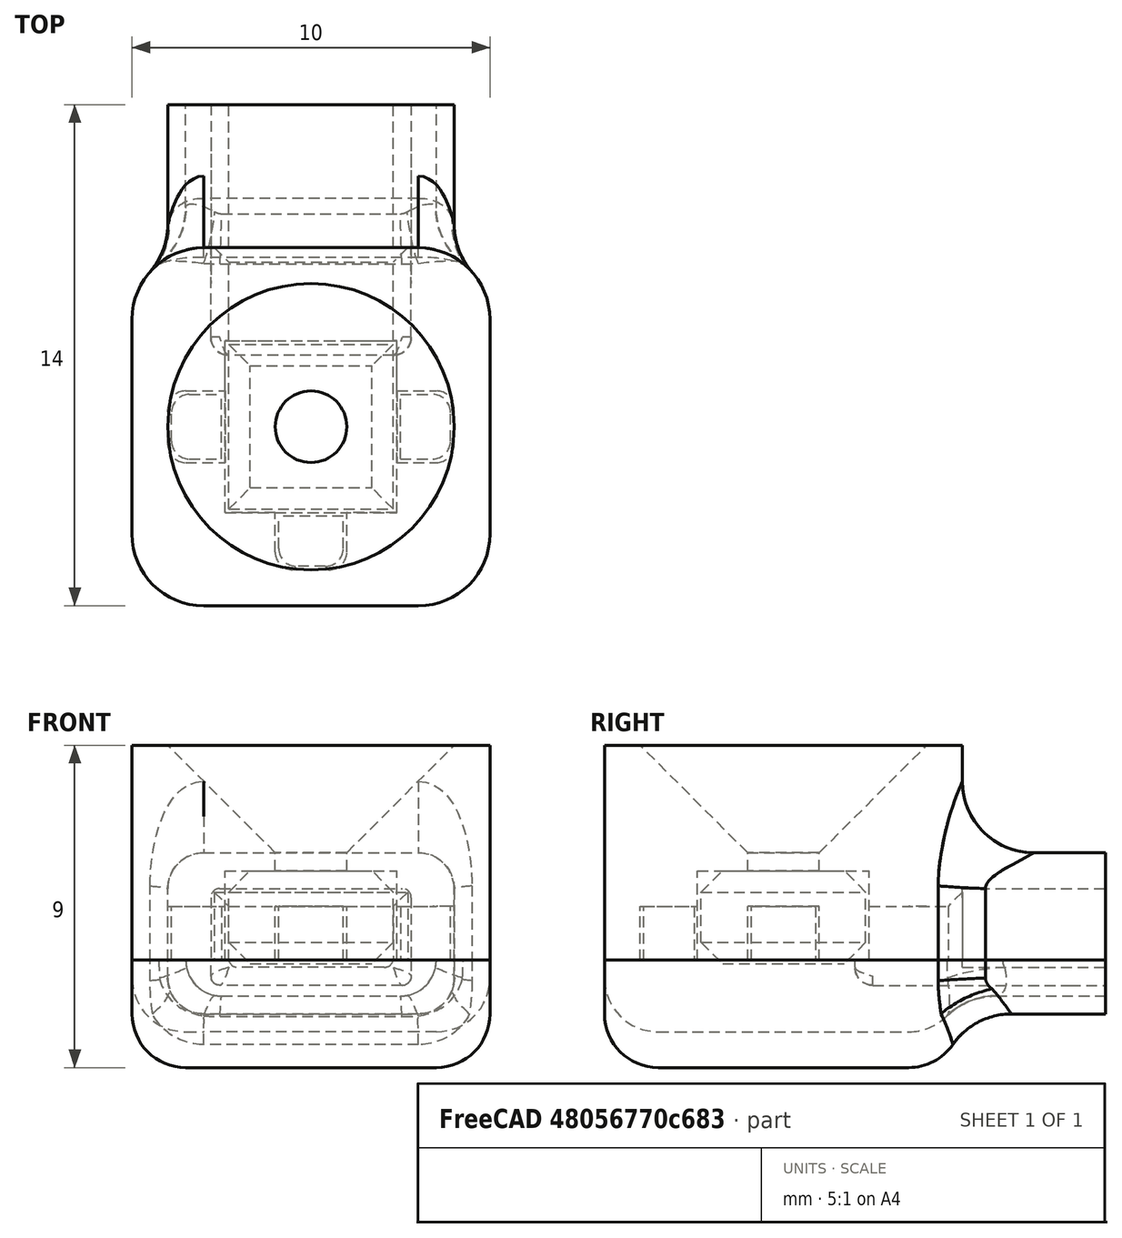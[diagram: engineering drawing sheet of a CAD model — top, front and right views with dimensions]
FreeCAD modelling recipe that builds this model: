
FCSTD DOCUMENT  (FreeCAD 0.18R16110 (Git))
Label: PhotodidoeHolder_APM_v4
License: All rights reserved
LicenseURL: http://en.wikipedia.org/wiki/All_rights_reserved
objects: Part::Box×24, Part::Fillet×22, Part::Cut×14, Part::MultiFuse×8, Part::Chamfer×2, Part::Cone×1, Part::Cylinder×1
note: 72 computed .brp shape members not serialized (recipe doc carries the construction recipe); baked Part::Feature solids carry a one-line shape summary decoded from their .brp

FEATURE [Part::Cone] Cone
  Angle = 360
  AttacherType = Attacher::AttachEngine3D
  Height = 3
  Radius1 = 1
  Radius2 = 4
FEATURE [Part::Box] Box  label="Cube"
  AttacherType = Attacher::AttachEngine3D
  Height = 3.5
  Length = 4.8
  Placement = pos=(-2.4,-2.4,-4) rot=(0,0,1;0rad)
  Width = 4.8
FEATURE [Part::Box] Box001  label="Cube001"
  AttacherType = Attacher::AttachEngine3D
  Height = 6
  Length = 10
  Placement = pos=(-5,-5,-3) rot=(0,0,1;0rad)
  Width = 10
FEATURE [Part::MultiFuse] Fusion
  Shapes = -> [Box,Cone]
FEATURE [Part::Cut] Cut
  Base = -> Box001
  Tool = -> Fusion
FEATURE [Part::Box] Box002  label="Cube002"
  AttacherType = Attacher::AttachEngine3D
  Height = 2
  Length = 4.6
  Placement = pos=(-2.3,2.4,-3.5) rot=(0,0,1;0rad)
  Width = 5
FEATURE [Part::Cut] Cut001
  Base = -> Cut
  Tool = -> Box002
FEATURE [Part::Fillet] Fillet
  Base = -> Cut001
  Edges = 4 edges r=2: [Edge1,Edge3,Edge6,Edge16]
FEATURE [Part::Cylinder] Cylinder
  Angle = 360
  AttacherType = Attacher::AttachEngine3D
  Height = 10
  Placement = pos=(0,0,-3) rot=(0,0,1;0rad)
  Radius = 1
FEATURE [Part::Cut] Cut002
  Base = -> Fillet
  Tool = -> Cylinder
FEATURE [Part::Box] Box003  label="Cube003"
  AttacherType = Attacher::AttachEngine3D
  Height = 3
  Length = 10
  Placement = pos=(-5,-5,-6) rot=(0,0,1;0rad)
  Width = 10
FEATURE [Part::Fillet] Fillet001
  Base = -> Box003
  Edges = 4 edges r=2: [Edge1,Edge3,Edge5,Edge7]
FEATURE [Part::Box] Box005  label="Diode"
  AttacherType = Attacher::AttachEngine3D
  Height = 2.6
  Length = 4.6
  Placement = pos=(-2.3,-2.3,-3) rot=(0,0,1;0rad)
  Width = 4.6
FEATURE [Part::Chamfer] Chamfer  label="Photodiode"
  Base = -> Box005
  Edges = 8 edges r=0.6: [Edge2,Edge4,Edge6,Edge8,Edge9,Edge10,Edge11,Edge12]
  Placement = pos=(0,0,-0.1) rot=(0,0,1;0rad)
FEATURE [Part::Fillet] Fillet003
  Base = -> Fillet001
  Edges = 8 edges r=1.5: [Edge4,Edge12,Edge14,Edge16,Edge17,Edge18,Edge19,Edge20]
FEATURE [Part::Box] Box007  label="Cube006"
  AttacherType = Attacher::AttachEngine3D
  Height = 1.5
  Length = 8
  Placement = pos=(-4,-1,-3) rot=(0,0,1;0rad)
  Width = 2
FEATURE [Part::Fillet] Fillet004
  Base = -> Box007
  Edges = 4 edges r=0.5: [Edge1,Edge3,Edge5,Edge7]
FEATURE [Part::Cut] Cut004
  Base = -> Cut002
  Tool = -> Fillet004
FEATURE [Part::Box] Box008  label="Cube007"
  AttacherType = Attacher::AttachEngine3D
  Height = 1.5
  Length = 7.8
  Placement = pos=(-3.9,-0.9,-3) rot=(0,0,1;0rad)
  Width = 1.8
FEATURE [Part::Fillet] Fillet005
  Base = -> Box008
  Edges = 4 edges r=0.5: [Edge1,Edge3,Edge5,Edge7]
FEATURE [Part::Box] Box009  label="Cube008"
  AttacherType = Attacher::AttachEngine3D
  Height = 1.5
  Length = 7.8
  Placement = pos=(-3.9,-0.9,-3) rot=(0,0,1;0rad)
  Width = 1.8
FEATURE [Part::Fillet] Fillet006
  Base = -> Box009
  Edges = 4 edges r=0.5: [Edge1,Edge3,Edge5,Edge7]
  Placement = pos=(0,0,0) rot=(0,0,1;1.5708rad)
FEATURE [Part::MultiFuse] Fusion001
  Shapes = -> [Fillet006,Fillet005]
FEATURE [Part::Box] Box010  label="Cube009"
  AttacherType = Attacher::AttachEngine3D
  Height = 5
  Length = 5
  Placement = pos=(-2.5,-2.5,-4) rot=(0,0,1;0rad)
  Width = 7
FEATURE [Part::Cut] Cut005
  Base = -> Fusion001
  Tool = -> Box010
FEATURE [Part::MultiFuse] Fusion002  label="Back"
  Shapes = -> [Fillet003,Cut005]
FEATURE [Part::Box] Box011  label="Cube010"
  AttacherType = Attacher::AttachEngine3D
  Height = 1.5
  Length = 8
  Placement = pos=(-4,-1,-3) rot=(0,0,1;0rad)
  Width = 2
FEATURE [Part::Fillet] Fillet007
  Base = -> Box011
  Edges = 4 edges r=0.5: [Edge1,Edge3,Edge5,Edge7]
  Placement = pos=(0,0,0) rot=(0,0,1;1.5708rad)
FEATURE [Part::Cut] Cut006
  Base = -> Cut004
  Tool = -> Fillet007
FEATURE [Part::Box] Box012  label="Cube011"
  AttacherType = Attacher::AttachEngine3D
  Height = 4.5
  Length = 8
  Placement = pos=(-4,4,-4.5) rot=(0,0,1;0rad)
  Width = 5
FEATURE [Part::Fillet] Fillet008
  Base = -> Box012
  Edges = 4 edges r=1: [Edge2,Edge4,Edge6,Edge8]
FEATURE [Part::Box] Box013  label="Cube012"
  AttacherType = Attacher::AttachEngine3D
  Height = 2.7
  Length = 5.6
  Placement = pos=(-2.8,4,-3.6) rot=(0,0,1;0rad)
  Width = 6
FEATURE [Part::Fillet] Fillet009
  Base = -> Box013
  Edges = 4 edges r=0.25: [Edge2,Edge4,Edge6,Edge8]
  Placement = pos=(0,0,-0.1) rot=(0,0,1;0rad)
FEATURE [Part::Cut] Cut007  label="Port"
  Base = -> Fillet008
  Tool = -> Fillet009
FEATURE [Part::Box] Box016  label="Cube015"
  AttacherType = Attacher::AttachEngine3D
  Height = 10
  Length = 10
  Placement = pos=(-5,1,-13) rot=(0,0,1;0rad)
  Width = 10
FEATURE [Part::Box] Box017  label="Cube016"
  AttacherType = Attacher::AttachEngine3D
  Height = 2.7
  Length = 5.6
  Placement = pos=(-2.8,4,-3.6) rot=(0,0,1;0rad)
  Width = 6
FEATURE [Part::Fillet] Fillet011
  Base = -> Box017
  Edges = 4 edges r=0.25: [Edge2,Edge4,Edge6,Edge8]
  Placement = pos=(0,0,-0.1) rot=(0,0,1;0rad)
FEATURE [Part::Box] Box018  label="Cube017"
  AttacherType = Attacher::AttachEngine3D
  Height = 4.5
  Length = 8
  Placement = pos=(-4,4,-4.5) rot=(0,0,1;0rad)
  Width = 5
FEATURE [Part::Fillet] Fillet010
  Base = -> Box018
  Edges = 4 edges r=1: [Edge2,Edge4,Edge6,Edge8]
FEATURE [Part::Cut] Cut008  label="Port001"
  Base = -> Fillet010
  Tool = -> Fillet011
FEATURE [Part::Box] Box019  label="Cube018"
  AttacherType = Attacher::AttachEngine3D
  Height = 10
  Length = 10
  Placement = pos=(-5,1,-3) rot=(0,0,1;0rad)
  Width = 10
FEATURE [Part::Cut] Cut009
  Base = -> Cut007
  Tool = -> Box016
FEATURE [Part::Cut] Cut010
  Base = -> Cut008
  Tool = -> Box019
FEATURE [Part::MultiFuse] Fusion003
  Shapes = -> [Cut010,Fusion002]
FEATURE [Part::MultiFuse] Fusion004
  Shapes = -> [Cut006,Cut009]
FEATURE [Part::Fillet] Fillet012  label="Case"
  Base = -> Fusion004
  Edges = 7 edges r=2: [Edge16,Edge17,Edge53,Edge54,Edge55,Edge58,Edge59]
FEATURE [Part::Fillet] Fillet013  label="CaseBack"
  Base = -> Fusion003
  Edges = 7 edges r=2: [Edge41,Edge49,Edge96,Edge97,Edge114,Edge115,Edge126]
FEATURE [Part::Box] Box020  label="Cube019"
  AttacherType = Attacher::AttachEngine3D
  Height = 2.7
  Length = 5.6
  Placement = pos=(-2.8,4,-3.6) rot=(0,0,1;0rad)
  Width = 6
FEATURE [Part::Fillet] Fillet014
  Base = -> Box020
  Edges = 4 edges r=0.25: [Edge2,Edge4,Edge6,Edge8]
  Placement = pos=(0,-2,-0.1) rot=(0,0,1;0rad)
FEATURE [Part::Box] Box021  label="Cube020"
  AttacherType = Attacher::AttachEngine3D
  Height = 1.5
  Length = 7.8
  Placement = pos=(-3.9,-0.9,-3) rot=(0,0,1;0rad)
  Width = 1.8
FEATURE [Part::Box] Box022  label="Cube021"
  AttacherType = Attacher::AttachEngine3D
  Height = 3
  Length = 10
  Placement = pos=(-5,-5,-6) rot=(0,0,1;0rad)
  Width = 10
FEATURE [Part::Box] Box023  label="Cube022"
  AttacherType = Attacher::AttachEngine3D
  Height = 1.5
  Length = 7.8
  Placement = pos=(-3.9,-0.9,-3) rot=(0,0,1;0rad)
  Width = 1.8
FEATURE [Part::Box] Box024  label="Cube023"
  AttacherType = Attacher::AttachEngine3D
  Height = 5
  Length = 5
  Placement = pos=(-2.5,-2.5,-4) rot=(0,0,1;0rad)
  Width = 7
FEATURE [Part::Box] Box025  label="Cube024"
  AttacherType = Attacher::AttachEngine3D
  Height = 2.7
  Length = 5.6
  Placement = pos=(-2.8,4,-3.6) rot=(0,0,1;0rad)
  Width = 6
FEATURE [Part::Box] Box026  label="Cube025"
  AttacherType = Attacher::AttachEngine3D
  Height = 4.5
  Length = 8
  Placement = pos=(-4,4,-4.5) rot=(0,0,1;0rad)
  Width = 5
FEATURE [Part::Box] Box027  label="Cube026"
  AttacherType = Attacher::AttachEngine3D
  Height = 10
  Length = 10
  Placement = pos=(-5,1,-3) rot=(0,0,1;0rad)
  Width = 10
FEATURE [Part::Fillet] Fillet015
  Base = -> Box022
  Edges = 4 edges r=2: [Edge1,Edge3,Edge5,Edge7]
FEATURE [Part::Fillet] Fillet016
  Base = -> Fillet015
  Edges = 8 edges r=1.5: [Edge4,Edge12,Edge14,Edge16,Edge17,Edge18,Edge19,Edge20]
FEATURE [Part::Fillet] Fillet017
  Base = -> Box021
  Edges = 4 edges r=0.5: [Edge1,Edge3,Edge5,Edge7]
FEATURE [Part::Fillet] Fillet018
  Base = -> Box023
  Edges = 4 edges r=0.5: [Edge1,Edge3,Edge5,Edge7]
  Placement = pos=(0,0,0) rot=(0,0,1;1.5708rad)
FEATURE [Part::MultiFuse] Fusion005
  Shapes = -> [Fillet018,Fillet017]
FEATURE [Part::Cut] Cut011
  Base = -> Fusion005
  Tool = -> Box024
FEATURE [Part::MultiFuse] Fusion006  label="Back001"
  Shapes = -> [Fillet016,Cut011]
FEATURE [Part::Fillet] Fillet019
  Base = -> Box026
  Edges = 4 edges r=1: [Edge2,Edge4,Edge6,Edge8]
FEATURE [Part::Fillet] Fillet020
  Base = -> Box025
  Edges = 4 edges r=0.25: [Edge2,Edge4,Edge6,Edge8]
  Placement = pos=(0,0,-0.1) rot=(0,0,1;0rad)
FEATURE [Part::Cut] Cut012  label="Port002"
  Base = -> Fillet019
  Tool = -> Fillet020
FEATURE [Part::Cut] Cut013
  Base = -> Cut012
  Tool = -> Box027
FEATURE [Part::MultiFuse] Fusion007
  Shapes = -> [Cut013,Fusion006]
FEATURE [Part::Cut] Cut014
  Base = -> Fusion007
  Tool = -> Fillet014
FEATURE [Part::Fillet] Fillet021
  Base = -> Cut014
  Edges = 5 edges r=2: [Edge57,Edge68,Edge76,Edge77,Edge123]
FEATURE [Part::Fillet] Fillet022
  Base = -> Fillet021
  Edges = 5 edges r=0.5: [Edge96,Edge100,Edge101,Edge102,Edge103]
FEATURE [Part::Chamfer] Chamfer001
  Base = -> Fillet012
  Edges = 3 edges r=0.4: [Edge89,Edge90,Edge91]
